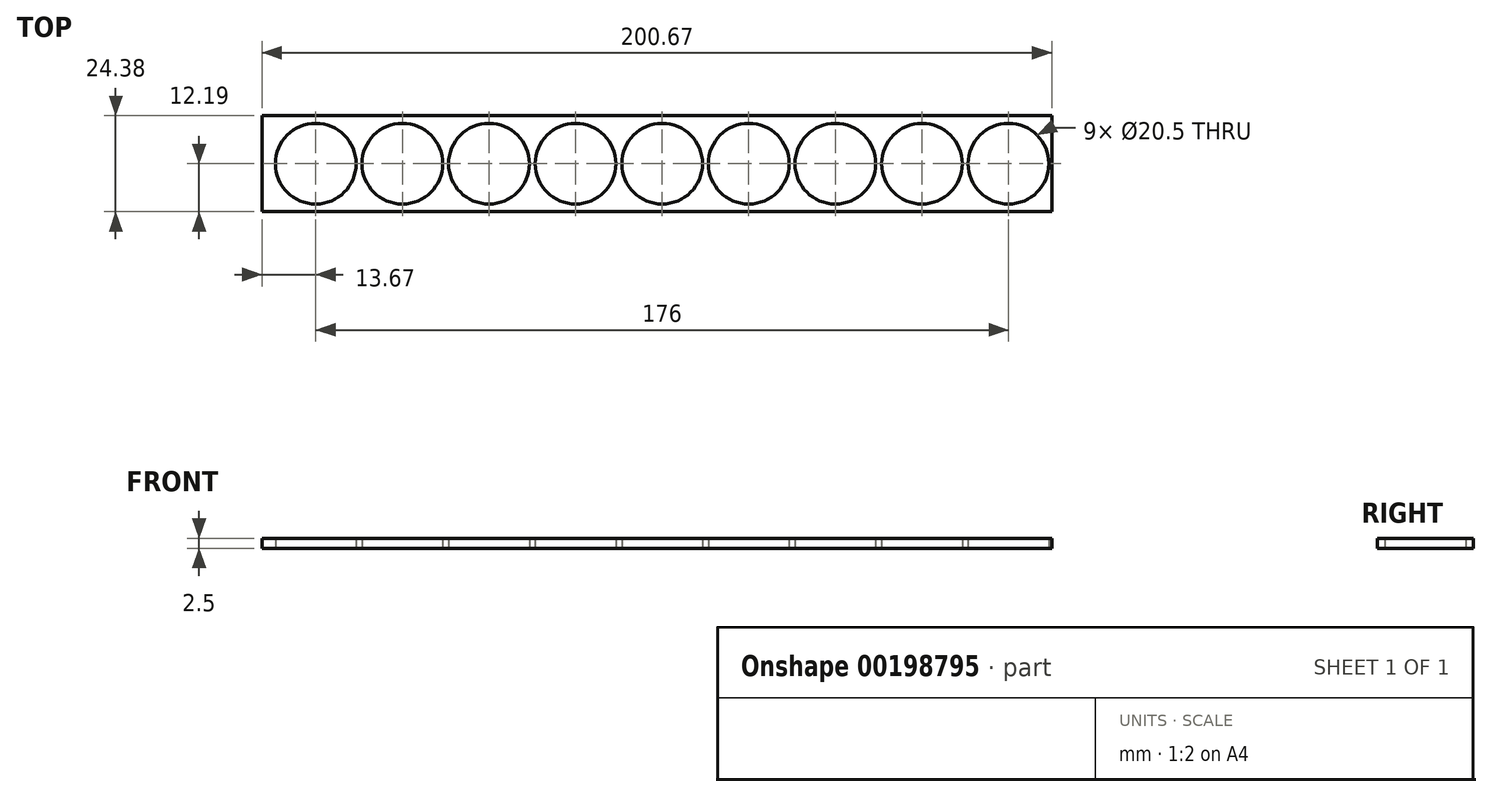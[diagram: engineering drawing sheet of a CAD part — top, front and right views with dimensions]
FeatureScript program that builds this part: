
annotation { "Feature Type Name" : "Feature", "Feature Type Description" : "" }
export const myFeature = defineFeature(function(context is Context, id is Id, definition is map)
    precondition{}
    {
        {
            var Q0;
            Q0=qCreatedBy(makeId("Top.planeOp"),FACE);
            var sketch = newSketch(context, id + "F0", { "sketchPlane" : qUnion([Q0])});
            skArc(sketch, "E0", {"start": v(-6.99, 7.5) * mm, "mid": v(-10.25, 0) * mm, "end": v(-6.99, -7.5) * mm});
            skLineSegment(sketch, "E1", {"start": v(-6.99, 7.5) * mm, "end": v(-6.99, -7.5) * mm, "construction": true});
            skLineSegment(sketch, "E2", {"start": v(6.99, 7.5) * mm, "end": v(6.99, -7.5) * mm, "construction": true});
            skArc(sketch, "E3.trimOffspring", {"start": v(6.99, -7.5) * mm, "mid": v(10.25, 0) * mm, "end": v(6.99, 7.5) * mm});
            skArc(sketch, "E4.1.0.0", {"start": v(15.01, 7.5) * mm, "mid": v(11.75, 0) * mm, "end": v(15.01, -7.5) * mm});
            skArc(sketch, "E4.1.0.2", {"start": v(28.99, -7.5) * mm, "mid": v(32.25, 0) * mm, "end": v(28.99, 7.5) * mm});
            skArc(sketch, "E4.2.0.0", {"start": v(37.01, 7.5) * mm, "mid": v(33.75, 0) * mm, "end": v(37.01, -7.5) * mm});
            skArc(sketch, "E4.2.0.2", {"start": v(50.99, -7.5) * mm, "mid": v(54.25, 0) * mm, "end": v(50.99, 7.5) * mm});
            skArc(sketch, "E4.3.0.0", {"start": v(59.01, 7.5) * mm, "mid": v(55.75, 0) * mm, "end": v(59.01, -7.5) * mm});
            skArc(sketch, "E4.3.0.2", {"start": v(72.99, -7.5) * mm, "mid": v(76.25, 0) * mm, "end": v(72.99, 7.5) * mm});
            skArc(sketch, "E4.4.0.0", {"start": v(81.01, 7.5) * mm, "mid": v(77.75, 0) * mm, "end": v(81.01, -7.5) * mm});
            skArc(sketch, "E4.4.0.2", {"start": v(94.99, -7.5) * mm, "mid": v(98.25, 0) * mm, "end": v(94.99, 7.5) * mm});
            skArc(sketch, "E4.5.0.0", {"start": v(103.01, 7.5) * mm, "mid": v(99.75, 0) * mm, "end": v(103.01, -7.5) * mm});
            skArc(sketch, "E4.5.0.2", {"start": v(116.99, -7.5) * mm, "mid": v(120.25, 0) * mm, "end": v(116.99, 7.5) * mm});
            skArc(sketch, "E4.6.0.0", {"start": v(125.01, 7.5) * mm, "mid": v(121.75, 0) * mm, "end": v(125.01, -7.5) * mm});
            skArc(sketch, "E4.6.0.2", {"start": v(138.99, -7.5) * mm, "mid": v(142.25, 0) * mm, "end": v(138.99, 7.5) * mm});
            skArc(sketch, "E4.7.0.0", {"start": v(147.01, 7.5) * mm, "mid": v(143.75, 0) * mm, "end": v(147.01, -7.5) * mm});
            skArc(sketch, "E4.7.0.2", {"start": v(160.99, -7.5) * mm, "mid": v(164.25, 0) * mm, "end": v(160.99, 7.5) * mm});
            skArc(sketch, "E4.8.0.0", {"start": v(169.01, 7.5) * mm, "mid": v(165.75, 0) * mm, "end": v(169.01, -7.5) * mm});
            skArc(sketch, "E4.8.0.2", {"start": v(182.99, -7.5) * mm, "mid": v(186.25, 0) * mm, "end": v(182.99, 7.5) * mm});
            skLineSegment(sketch, "E4.direction1", {"start": v(6.99, -7.5) * mm, "end": v(15.01, -7.5) * mm, "construction": true});
            skLineSegment(sketch, "E5.bottom", {"start": v(-13.67, 12.2) * mm, "end": v(187, 12.2) * mm});
            skLineSegment(sketch, "E5.top", {"start": v(-13.67, -12.2) * mm, "end": v(187, -12.2) * mm});
            skLineSegment(sketch, "E5.left", {"start": v(-13.67, 12.2) * mm, "end": v(-13.67, -12.2) * mm});
            skLineSegment(sketch, "E5.right", {"start": v(187, 12.2) * mm, "end": v(187, -12.2) * mm});
            skLineSegment(sketch, "E6", {"start": v(0, 0) * mm, "end": v(22, 0) * mm, "construction": true});
            skPoint(sketch, "E7", {"position": v(11, 0) * mm});
            skArc(sketch, "E8", {"start": v(6.99, 7.5) * mm, "mid": v(0, 10.25) * mm, "end": v(-6.99, 7.5) * mm});
            skArc(sketch, "E9.trimOffspring", {"start": v(-6.99, -7.5) * mm, "mid": v(0, -10.25) * mm, "end": v(6.99, -7.5) * mm});
            skArc(sketch, "E10.1.0.0", {"start": v(28.99, 7.5) * mm, "mid": v(22, 10.25) * mm, "end": v(15.01, 7.5) * mm});
            skArc(sketch, "E10.1.0.1", {"start": v(15.01, -7.5) * mm, "mid": v(22, -10.25) * mm, "end": v(28.99, -7.5) * mm});
            skArc(sketch, "E10.2.0.0", {"start": v(50.99, 7.5) * mm, "mid": v(44, 10.25) * mm, "end": v(37.01, 7.5) * mm});
            skArc(sketch, "E10.2.0.1", {"start": v(37.01, -7.5) * mm, "mid": v(44, -10.25) * mm, "end": v(50.99, -7.5) * mm});
            skArc(sketch, "E10.3.0.0", {"start": v(72.99, 7.5) * mm, "mid": v(66, 10.25) * mm, "end": v(59.01, 7.5) * mm});
            skArc(sketch, "E10.3.0.1", {"start": v(59.01, -7.5) * mm, "mid": v(66, -10.25) * mm, "end": v(72.99, -7.5) * mm});
            skArc(sketch, "E10.4.0.0", {"start": v(94.99, 7.5) * mm, "mid": v(88, 10.25) * mm, "end": v(81.01, 7.5) * mm});
            skArc(sketch, "E10.4.0.1", {"start": v(81.01, -7.5) * mm, "mid": v(88, -10.25) * mm, "end": v(94.99, -7.5) * mm});
            skArc(sketch, "E10.5.0.0", {"start": v(116.99, 7.5) * mm, "mid": v(110, 10.25) * mm, "end": v(103.01, 7.5) * mm});
            skArc(sketch, "E10.5.0.1", {"start": v(103.01, -7.5) * mm, "mid": v(110, -10.25) * mm, "end": v(116.99, -7.5) * mm});
            skArc(sketch, "E10.6.0.0", {"start": v(138.99, 7.5) * mm, "mid": v(132, 10.25) * mm, "end": v(125.01, 7.5) * mm});
            skArc(sketch, "E10.6.0.1", {"start": v(125.01, -7.5) * mm, "mid": v(132, -10.25) * mm, "end": v(138.99, -7.5) * mm});
            skArc(sketch, "E10.7.0.0", {"start": v(160.99, 7.5) * mm, "mid": v(154, 10.25) * mm, "end": v(147.01, 7.5) * mm});
            skArc(sketch, "E10.7.0.1", {"start": v(147.01, -7.5) * mm, "mid": v(154, -10.25) * mm, "end": v(160.99, -7.5) * mm});
            skArc(sketch, "E10.8.0.0", {"start": v(182.99, 7.5) * mm, "mid": v(176, 10.25) * mm, "end": v(169.01, 7.5) * mm});
            skArc(sketch, "E10.8.0.1", {"start": v(169.01, -7.5) * mm, "mid": v(176, -10.25) * mm, "end": v(182.99, -7.5) * mm});
            skSolve(sketch);
        }
        {
            var Q0;
            Q0=qSketchRegion(id+"F0",true);
            extrude(context, id + "F1", {"entities" : qUnion([Q0]), "depth" : 2.5 * mm});
        }
    });
